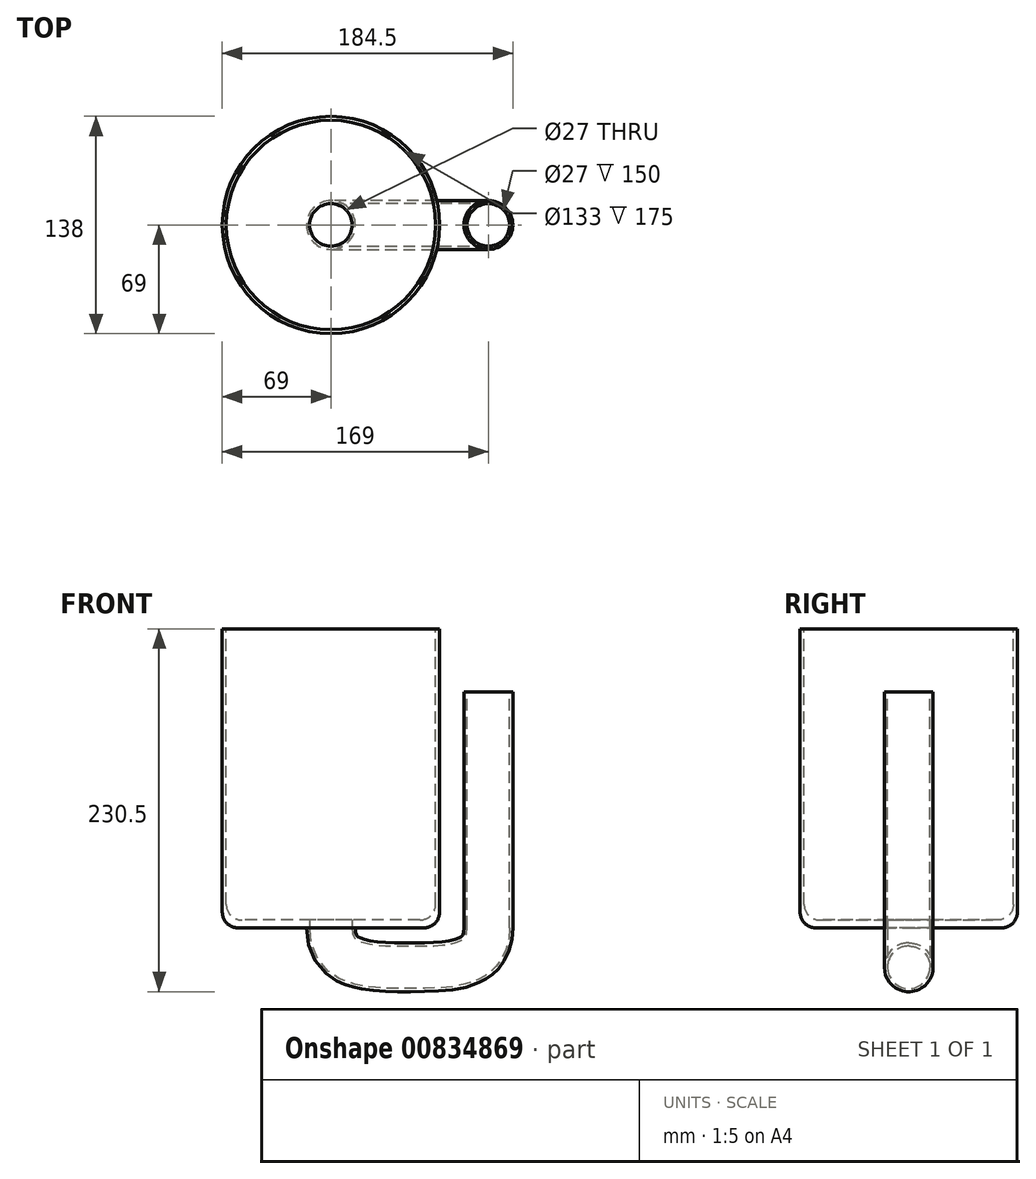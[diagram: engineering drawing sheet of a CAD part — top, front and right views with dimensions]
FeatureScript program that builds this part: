
annotation { "Feature Type Name" : "Feature", "Feature Type Description" : "" }
export const myFeature = defineFeature(function(context is Context, id is Id, definition is map)
    precondition{}
    {
        {
            var Q0;
            Q0=qCreatedBy(makeId("Front.planeOp"),FACE);
            var sketch = newSketch(context, id + "F0", { "sketchPlane" : qUnion([Q0])});
            skFitSpline(sketch, "E0", {"points": [v(-50, 25) * mm, v(0, 0) * mm, v(50, 25) * mm], "startDerivative": vector(0, -150) * mm, "endDerivative": vector(0, 150) * mm});
            skLineSegment(sketch, "E1", {"start": v(-50, 25) * mm, "end": v(-50, 0) * mm, "construction": true});
            skLineSegment(sketch, "E2", {"start": v(50, 25) * mm, "end": v(50, 0) * mm, "construction": true});
            skLineSegment(sketch, "E3", {"start": v(50, 25) * mm, "end": v(50, 175) * mm});
            skSolve(sketch);
        }
        {
            var Q0;
            Q0=qCreatedBy(makeId("Top.planeOp"),FACE);
            var Q1;
            Q1=sQuery(id+"F0.wireOp",VERTEX,"E0.start");
            cPlane(context, id + "F1", {"entities" : qUnion([Q0, Q1]), "cplaneType" : CPlaneType.PLANE_POINT, "offset" : 25 * mm, "width" : 150 * mm, "height" : 150 * mm});
        }
        {
            var Q0;
            Q0=qCreatedBy(id+"F1.planeOp",FACE);
            var sketch = newSketch(context, id + "F2", { "sketchPlane" : qUnion([Q0])});
            skPoint(sketch, "E4.0", {"position": v(-50, 0) * mm});
            skCircle(sketch, "E5", {"center": v(-50, 0) * mm, "radius": 13.5 * mm});
            skCircle(sketch, "E6", {"center": v(-50, 0) * mm, "radius": 15.5 * mm});
            skSolve(sketch);
        }
        {
            var Q0;
            Q0=makeQuery(id+"F2.imprint","IMPRINT",FACE,{"disambiguationData":[TD([[makeQuery(id+"F2.imprint","IMPRINT",EDGE,{"derivedFrom":sQuery(id+"F2.wireOp",EDGE,"E5")}),-1.0]])]});
            var Q1;
            Q1=sQuery(id+"F0.wireOp",EDGE,"2JODRv6S-TYKI-78hx-53Cv-C6PpvcCdArXI");
            var Q2;
            Q2=sQuery(id+"F0.wireOp",EDGE,"E0");
            var Q3;
            Q3=sQuery(id+"F0.wireOp",EDGE,"E3");
            sweep(context, id + "F3", {"profiles" : qUnion([Q0]), "path" : qUnion([Q1, Q2, Q3])});
        }
        {
            var Q0;
            Q0=makeQuery(id+"F2.imprint","IMPRINT",FACE,{"disambiguationData":[TD([[makeQuery(id+"F2.imprint","IMPRINT",EDGE,{"derivedFrom":sQuery(id+"F2.wireOp",EDGE,"E5")}),-1.0]])]});
            var sketch = newSketch(context, id + "F4", { "sketchPlane" : qUnion([Q0])});
            skPoint(sketch, "E7.0", {"position": v(-50, 0) * mm});
            skCircle(sketch, "E8", {"center": v(-50, 0) * mm, "radius": 69 * mm});
            skSolve(sketch);
        }
        {
            var Q0;
            Q0=makeQuery(id+"F2.imprint","IMPRINT",FACE,{"disambiguationData":[TD([[makeQuery(id+"F2.imprint","IMPRINT",EDGE,{"derivedFrom":sQuery(id+"F2.wireOp",EDGE,"E5")}),-1.0]])]});
            var Q1;
            Q1=makeQuery(id+"F4.imprint","IMPRINT",FACE,{"disambiguationData":[TD([[makeQuery(id+"F4.imprint","IMPRINT",EDGE,{"derivedFrom":sQuery(id+"F4.wireOp",EDGE,"E8")}),1.0]])]});
            extrude(context, id + "F5", {"entities" : qUnion([Q0, Q1]), "operationType" : NewBodyOperationType.ADD, "depth" : 190 * mm, "offsetDistance" : 25 * mm});
        }
        {
            var Q0;
            {var subQ0=sQuery(id+"F2.wireOp",EDGE,"E6");Q0=makeQuery(id+"F5.boolean.opBoolean","MERGE",FACE,{"derivedFrom":[makeQuery(id+"F5.opExtrude","CAP_FACE",FACE,{"disambiguationData":[OSD([sQuery(id+"F2.wireOp",EDGE,"E5"),subQ0])],"isStart":false}),makeQuery(id+"F5.opExtrude","CAP_FACE",FACE,{"disambiguationData":[OSD([subQ0,sQuery(id+"F4.wireOp",EDGE,"E8")])],"isStart":false})]});}
            var sketch = newSketch(context, id + "F6", { "sketchPlane" : qUnion([Q0])});
            skCircle(sketch, "E9", {"center": v(-50, 0) * mm, "radius": 66.5 * mm});
            skSolve(sketch);
        }
        {
            var Q0;
            Q0=makeQuery(id+"F6.imprint","IMPRINT",FACE,{"disambiguationData":[TD([[makeQuery(id+"F6.imprint","IMPRINT",EDGE,{"derivedFrom":sQuery(id+"F6.wireOp",EDGE,"E9")}),1.0]])]});
            extrude(context, id + "F7", {"entities" : qUnion([Q0]), "operationType" : NewBodyOperationType.REMOVE, "oppositeDirection" : true, "depth" : 185 * mm, "offsetDistance" : 25 * mm});
        }
        {
            var Q0;
            Q0=makeQuery(id+"F7.boolean.opBoolean","COPY",EDGE,{"derivedFrom":makeQuery(id+"F7.opExtrude","CAP_EDGE",EDGE,{"disambiguationData":[OSD([sQuery(id+"F6.wireOp",EDGE,"E9")])],"isStart":false})});
            var Q1;
            Q1=makeQuery(id+"F5.opExtrude","CAP_EDGE",EDGE,{"disambiguationData":[OSD([sQuery(id+"F4.wireOp",EDGE,"E8")])],"isStart":true});
            fillet(context, id + "F8", {"entities" : qUnion([Q0, Q1]), "radius" : 10 * mm, "tangentPropagation" : true, "allowEdgeOverflow" : false});
        }
    });
